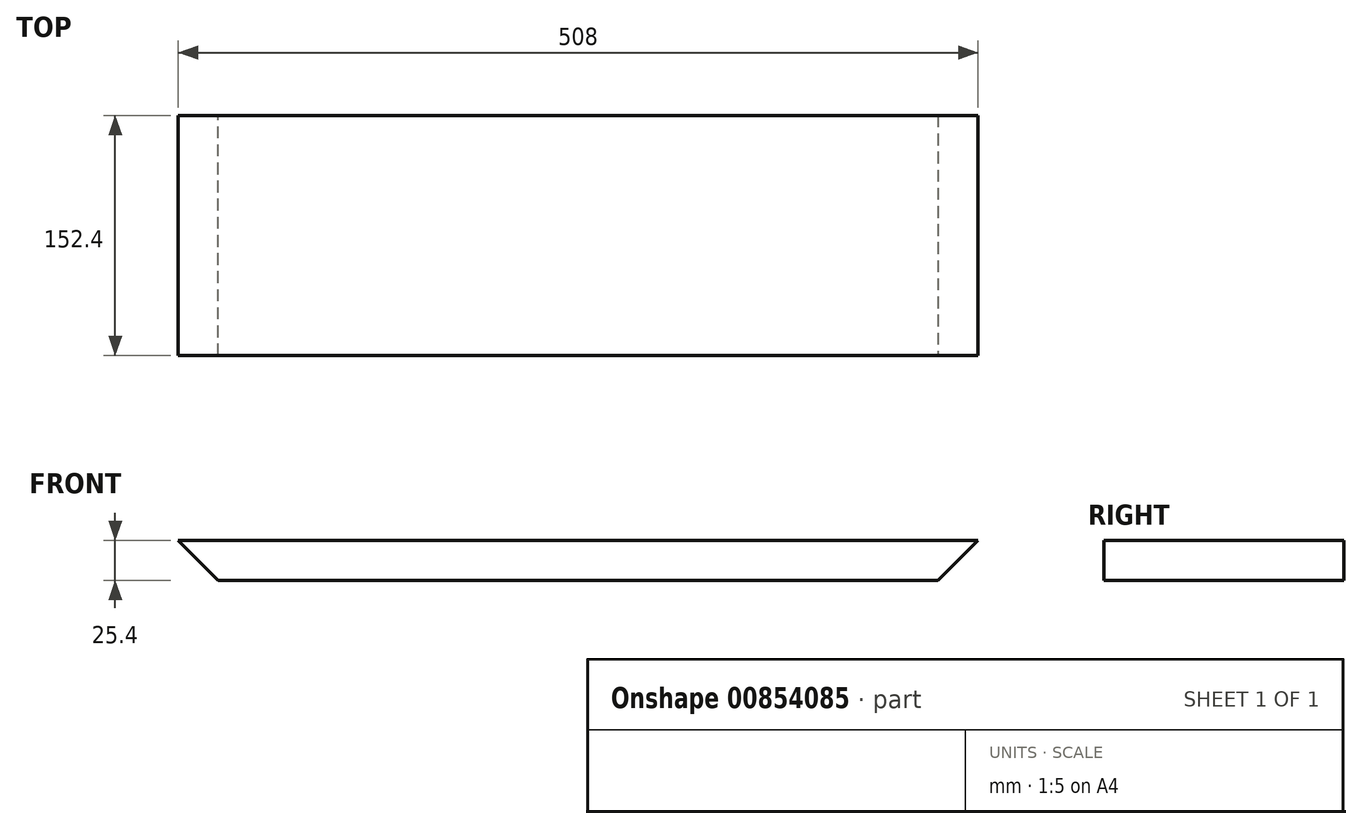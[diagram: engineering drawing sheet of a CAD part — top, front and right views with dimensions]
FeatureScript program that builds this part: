
annotation { "Feature Type Name" : "Feature", "Feature Type Description" : "" }
export const myFeature = defineFeature(function(context is Context, id is Id, definition is map)
    precondition{}
    {
        {
            var Q0;
            Q0=qCreatedBy(makeId("Front.planeOp"),FACE);
            var sketch = newSketch(context, id + "F0", { "sketchPlane" : qUnion([Q0])});
            skLineSegment(sketch, "E0.bottom", {"start": v(254, -12.7) * mm, "end": v(-254, -12.7) * mm});
            skLineSegment(sketch, "E0.top", {"start": v(254, 12.7) * mm, "end": v(-254, 12.7) * mm});
            skLineSegment(sketch, "E0.left", {"start": v(254, -12.7) * mm, "end": v(254, 12.7) * mm});
            skLineSegment(sketch, "E0.right", {"start": v(-254, -12.7) * mm, "end": v(-254, 12.7) * mm});
            skSolve(sketch);
        }
        {
            var Q0;
            Q0 = qSketchRegion(id + "F0", true);
            extrude(context, id + "F1", {"entities" : qUnion([Q0]), "depth" : 152.4 * mm, "offsetDistance" : 25.4 * mm});
        }
        {
            var Q0;
            Q0=makeQuery(id+"F1.opExtrude","SWEPT_EDGE",EDGE,{"disambiguationData":[OSD([sQuery(id+"F0.wireOp",EDGE,"E0.bottom"),sQuery(id+"F0.wireOp",EDGE,"E0.right")])]});
            var Q1;
            Q1=makeQuery(id+"F1.opExtrude","SWEPT_EDGE",EDGE,{"disambiguationData":[OSD([sQuery(id+"F0.wireOp",EDGE,"E0.bottom"),sQuery(id+"F0.wireOp",EDGE,"E0.left")])]});
            chamfer(context, id + "F2", {"entities" : qUnion([Q0, Q1]), "width" : 25.4 * mm, "tangentPropagation" : true});
        }
    });
